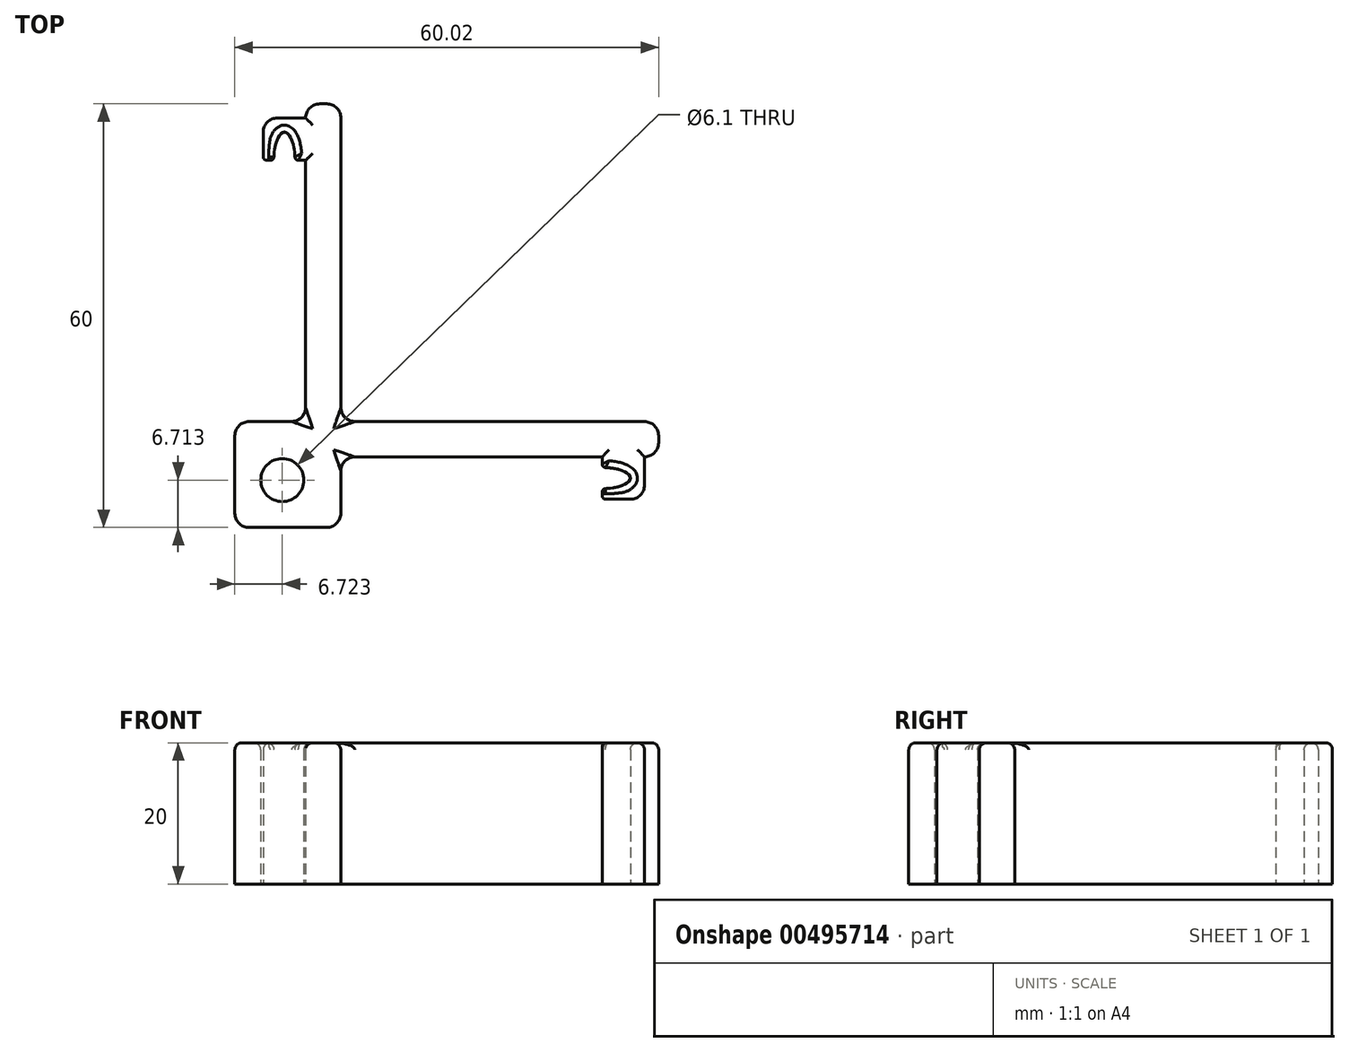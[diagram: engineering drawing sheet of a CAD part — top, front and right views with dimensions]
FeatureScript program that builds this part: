
annotation { "Feature Type Name" : "Feature", "Feature Type Description" : "" }
export const myFeature = defineFeature(function(context is Context, id is Id, definition is map)
    precondition{}
    {
        {
            var Q0;
            Q0=qCreatedBy(makeId("Top.planeOp"),FACE);
            var sketch = newSketch(context, id + "F0", { "sketchPlane" : qUnion([Q0]), "disableImprinting" : false});
            skLineSegment(sketch, "E0", {"start": v(50, 0) * mm, "end": v(4.98, 0) * mm});
            skLineSegment(sketch, "E1", {"start": v(0, 50) * mm, "end": v(5, 50) * mm});
            skLineSegment(sketch, "E2", {"start": v(5, 50) * mm, "end": v(5, 5) * mm});
            skLineSegment(sketch, "E3", {"start": v(5, 5) * mm, "end": v(50, 5) * mm});
            skLineSegment(sketch, "E4", {"start": v(50, 5) * mm, "end": v(50, 0) * mm});
            skLineSegment(sketch, "E5", {"start": v(4.98, 0) * mm, "end": v(4.98, 0) * mm});
            skLineSegment(sketch, "E6", {"start": v(4.98, -10) * mm, "end": v(-10.02, -10) * mm});
            skLineSegment(sketch, "E7", {"start": v(-10.02, -10) * mm, "end": v(-10.02, 5) * mm});
            skLineSegment(sketch, "E8", {"start": v(-10.02, 5) * mm, "end": v(0, 5) * mm});
            skLineSegment(sketch, "E9", {"start": v(5, 5) * mm, "end": v(-10.02, -10) * mm, "construction": true});
            skCircle(sketch, "E10", {"center": v(-3.3, -3.29) * mm, "radius": 3.05 * mm});
            skLineSegment(sketch, "E11", {"start": v(0, 5) * mm, "end": v(0, 50) * mm});
            skLineSegment(sketch, "E12", {"start": v(0, 5) * mm, "end": v(0, 5) * mm});
            skLineSegment(sketch, "E13", {"start": v(4.98, 0) * mm, "end": v(4.98, -10) * mm});
            skSolve(sketch);
        }
        {
            var Q0;
            Q0=qCreatedBy(makeId("Top.planeOp"),FACE);
            var sketch = newSketch(context, id + "F1", { "sketchPlane" : qUnion([Q0])});
            skLineSegment(sketch, "E14.bottom", {"start": v(0, 48) * mm, "end": v(-6, 48) * mm});
            skLineSegment(sketch, "E14.top", {"start": v(0, 42) * mm, "end": v(-1.5, 42) * mm});
            skLineSegment(sketch, "E14.left", {"start": v(0, 48) * mm, "end": v(0, 42) * mm});
            skLineSegment(sketch, "E14.right", {"start": v(-6, 48) * mm, "end": v(-6, 42) * mm});
            skLineSegment(sketch, "E15.bottom", {"start": v(48, 0) * mm, "end": v(42, 0) * mm});
            skLineSegment(sketch, "E15.top", {"start": v(48, -6) * mm, "end": v(42, -6) * mm});
            skLineSegment(sketch, "E15.left", {"start": v(48, 0) * mm, "end": v(48, -6) * mm});
            skLineSegment(sketch, "E15.right", {"start": v(42, 0) * mm, "end": v(42, -1.5) * mm});
            skEllipticalArc(sketch, "E16", {});
            skLineSegment(sketch, "E17", {"start": v(-4.5, 42) * mm, "end": v(-6, 42) * mm});
            skEllipticalArc(sketch, "E18", {});
            skLineSegment(sketch, "E19", {"start": v(42, -1.5) * mm, "end": v(42, -1.5) * mm});
            skLineSegment(sketch, "E20", {"start": v(42, -4.5) * mm, "end": v(42, -6) * mm});
            const initialGuessF1  = {"E16": [0.042, -0.003, -1, 0, 0.004, 0.0015, 1.5707963267948966, 4.71238898038469], "E18": [-0.003, 0.042, 0, -1, 0.004, 0.0015, 1.5707963267948966, 4.71238898038469]};
            skSetInitialGuess(sketch, initialGuessF1);
            skSolve(sketch);
        }
        {
            var Q0;
            Q0=makeQuery(id+"F0.imprint","IMPRINT",FACE,{"disambiguationData":[TD([[makeQuery(id+"F0.imprint","IMPRINT",EDGE,{"derivedFrom":sQuery(id+"F0.wireOp",EDGE,"E0")}),-1.0]])]});
            extrude(context, id + "F2", {"entities" : qUnion([Q0]), "depth" : 20 * mm});
        }
        {
            var Q0;
            Q0=makeQuery(id+"F1.imprint","IMPRINT",FACE,{"disambiguationData":[TD([[makeQuery(id+"F1.imprint","IMPRINT",EDGE,{"derivedFrom":sQuery(id+"F1.wireOp",EDGE,"E14.bottom")}),1.0]])]});
            var Q1;
            Q1=makeQuery(id+"F1.imprint","IMPRINT",FACE,{"disambiguationData":[TD([[makeQuery(id+"F1.imprint","IMPRINT",EDGE,{"derivedFrom":sQuery(id+"F1.wireOp",EDGE,"E15.bottom")}),1.0]])]});
            extrude(context, id + "F3", {"entities" : qUnion([Q0, Q1]), "operationType" : NewBodyOperationType.ADD, "depth" : 20 * mm});
        }
        {
            var Q0;
            Q0=makeQuery(id+"F3.boolean.opBoolean","MERGE",FACE,{"derivedFrom":[makeQuery(id+"F2.opExtrude","CAP_FACE",FACE,{"disambiguationData":[OSD([sQuery(id+"F0.wireOp",EDGE,"E0"),sQuery(id+"F0.wireOp",EDGE,"E1"),sQuery(id+"F0.wireOp",EDGE,"E2"),sQuery(id+"F0.wireOp",EDGE,"E3"),sQuery(id+"F0.wireOp",EDGE,"E4"),sQuery(id+"F0.wireOp",EDGE,"E6"),sQuery(id+"F0.wireOp",EDGE,"E7"),sQuery(id+"F0.wireOp",EDGE,"E8"),sQuery(id+"F0.wireOp",EDGE,"E10"),sQuery(id+"F0.wireOp",EDGE,"E11"),sQuery(id+"F0.wireOp",EDGE,"E13")])],"isStart":false}),makeQuery(id+"F3.opExtrude","CAP_FACE",FACE,{"disambiguationData":[OSD([sQuery(id+"F1.wireOp",EDGE,"E14.bottom"),sQuery(id+"F1.wireOp",EDGE,"E14.top"),sQuery(id+"F1.wireOp",EDGE,"E14.left"),sQuery(id+"F1.wireOp",EDGE,"E14.right"),sQuery(id+"F1.wireOp",EDGE,"E17"),sQuery(id+"F1.wireOp",EDGE,"E18")])],"isStart":false}),makeQuery(id+"F3.opExtrude","CAP_FACE",FACE,{"disambiguationData":[OSD([sQuery(id+"F1.wireOp",EDGE,"E15.bottom"),sQuery(id+"F1.wireOp",EDGE,"E15.top"),sQuery(id+"F1.wireOp",EDGE,"E15.left"),sQuery(id+"F1.wireOp",EDGE,"E15.right"),sQuery(id+"F1.wireOp",EDGE,"E16"),sQuery(id+"F1.wireOp",EDGE,"E20")])],"isStart":false})]});
            fillet(context, id + "F4", {"entities" : qUnion([Q0]), "radius" : 1 * mm, "tangentPropagation" : true, "allowEdgeOverflow" : false});
        }
        {
            var Q0;
            Q0=makeQuery(id+"F2.opExtrude","SWEPT_EDGE",EDGE,{"disambiguationData":[OSD([sQuery(id+"F0.wireOp",EDGE,"E6"),sQuery(id+"F0.wireOp",EDGE,"E13")])]});
            var Q1;
            Q1=makeQuery(id+"F2.opExtrude","SWEPT_EDGE",EDGE,{"disambiguationData":[OSD([sQuery(id+"F0.wireOp",EDGE,"E0"),sQuery(id+"F0.wireOp",EDGE,"E13")])]});
            var Q2;
            Q2=makeQuery(id+"F3.opExtrude","SWEPT_EDGE",EDGE,{"disambiguationData":[OSD([sQuery(id+"F1.wireOp",EDGE,"E15.top"),sQuery(id+"F1.wireOp",EDGE,"E15.left")])]});
            var Q3;
            Q3=makeQuery(id+"F2.opExtrude","SWEPT_EDGE",EDGE,{"disambiguationData":[OSD([sQuery(id+"F0.wireOp",EDGE,"E3"),sQuery(id+"F0.wireOp",EDGE,"E4")])]});
            var Q4;
            Q4=makeQuery(id+"F2.opExtrude","SWEPT_EDGE",EDGE,{"disambiguationData":[OSD([sQuery(id+"F0.wireOp",EDGE,"E2"),sQuery(id+"F0.wireOp",EDGE,"E3")])]});
            var Q5;
            Q5=makeQuery(id+"F2.opExtrude","SWEPT_EDGE",EDGE,{"disambiguationData":[OSD([sQuery(id+"F0.wireOp",EDGE,"E1"),sQuery(id+"F0.wireOp",EDGE,"E2")])]});
            var Q6;
            Q6=makeQuery(id+"F3.opExtrude","SWEPT_EDGE",EDGE,{"disambiguationData":[OSD([sQuery(id+"F1.wireOp",EDGE,"E14.bottom"),sQuery(id+"F1.wireOp",EDGE,"E14.right")])]});
            var Q7;
            Q7=makeQuery(id+"F2.opExtrude","SWEPT_EDGE",EDGE,{"disambiguationData":[OSD([sQuery(id+"F0.wireOp",EDGE,"E1"),sQuery(id+"F0.wireOp",EDGE,"E11")])]});
            var Q8;
            Q8=makeQuery(id+"F2.opExtrude","SWEPT_EDGE",EDGE,{"disambiguationData":[OSD([sQuery(id+"F0.wireOp",EDGE,"E6"),sQuery(id+"F0.wireOp",EDGE,"E7")])]});
            var Q9;
            Q9=makeQuery(id+"F2.opExtrude","SWEPT_EDGE",EDGE,{"disambiguationData":[OSD([sQuery(id+"F0.wireOp",EDGE,"E7"),sQuery(id+"F0.wireOp",EDGE,"E8")])]});
            var Q10;
            Q10=makeQuery(id+"F2.opExtrude","SWEPT_EDGE",EDGE,{"disambiguationData":[OSD([sQuery(id+"F0.wireOp",EDGE,"E8"),sQuery(id+"F0.wireOp",EDGE,"E11")])]});
            var Q11;
            Q11=makeQuery(id+"F2.opExtrude","SWEPT_EDGE",EDGE,{"disambiguationData":[OSD([sQuery(id+"F0.wireOp",EDGE,"E0"),sQuery(id+"F0.wireOp",EDGE,"E4")])]});
            fillet(context, id + "F5", {"entities" : qUnion([Q0, Q1, Q2, Q3, Q4, Q5, Q6, Q7, Q8, Q9, Q10, Q11]), "radius" : 2 * mm, "tangentPropagation" : true, "allowEdgeOverflow" : false});
        }
        {
            var Q0;
            Q0=makeQuery(id+"F3.opExtrude","SWEPT_EDGE",EDGE,{"disambiguationData":[OSD([sQuery(id+"F1.wireOp",EDGE,"E15.top"),sQuery(id+"F1.wireOp",EDGE,"E20")])]});
            var Q1;
            Q1=makeQuery(id+"F3.opExtrude","SWEPT_EDGE",EDGE,{"disambiguationData":[OSD([sQuery(id+"F1.wireOp",EDGE,"E16"),sQuery(id+"F1.wireOp",EDGE,"E20")])]});
            var Q2;
            Q2=makeQuery(id+"F3.opExtrude","SWEPT_EDGE",EDGE,{"disambiguationData":[OSD([sQuery(id+"F1.wireOp",EDGE,"E15.right"),sQuery(id+"F1.wireOp",EDGE,"E16")])]});
            var Q3;
            Q3=makeQuery(id+"F3.opExtrude","SWEPT_EDGE",EDGE,{"disambiguationData":[OSD([sQuery(id+"F1.wireOp",EDGE,"E15.bottom"),sQuery(id+"F1.wireOp",EDGE,"E15.right")])]});
            var Q4;
            Q4=makeQuery(id+"F3.opExtrude","SWEPT_EDGE",EDGE,{"disambiguationData":[OSD([sQuery(id+"F1.wireOp",EDGE,"E14.top"),sQuery(id+"F1.wireOp",EDGE,"E14.left")])]});
            var Q5;
            Q5=makeQuery(id+"F3.opExtrude","SWEPT_EDGE",EDGE,{"disambiguationData":[OSD([sQuery(id+"F1.wireOp",EDGE,"E14.top"),sQuery(id+"F1.wireOp",EDGE,"E18")])]});
            var Q6;
            Q6=makeQuery(id+"F3.opExtrude","SWEPT_EDGE",EDGE,{"disambiguationData":[OSD([sQuery(id+"F1.wireOp",EDGE,"E17"),sQuery(id+"F1.wireOp",EDGE,"E18")])]});
            var Q7;
            Q7=makeQuery(id+"F3.opExtrude","SWEPT_EDGE",EDGE,{"disambiguationData":[OSD([sQuery(id+"F1.wireOp",EDGE,"E14.right"),sQuery(id+"F1.wireOp",EDGE,"E17")])]});
            fillet(context, id + "F6", {"entities" : qUnion([Q0, Q1, Q2, Q3, Q4, Q5, Q6, Q7]), "radius" : .5 * mm, "tangentPropagation" : true, "allowEdgeOverflow" : false});
        }
    });
